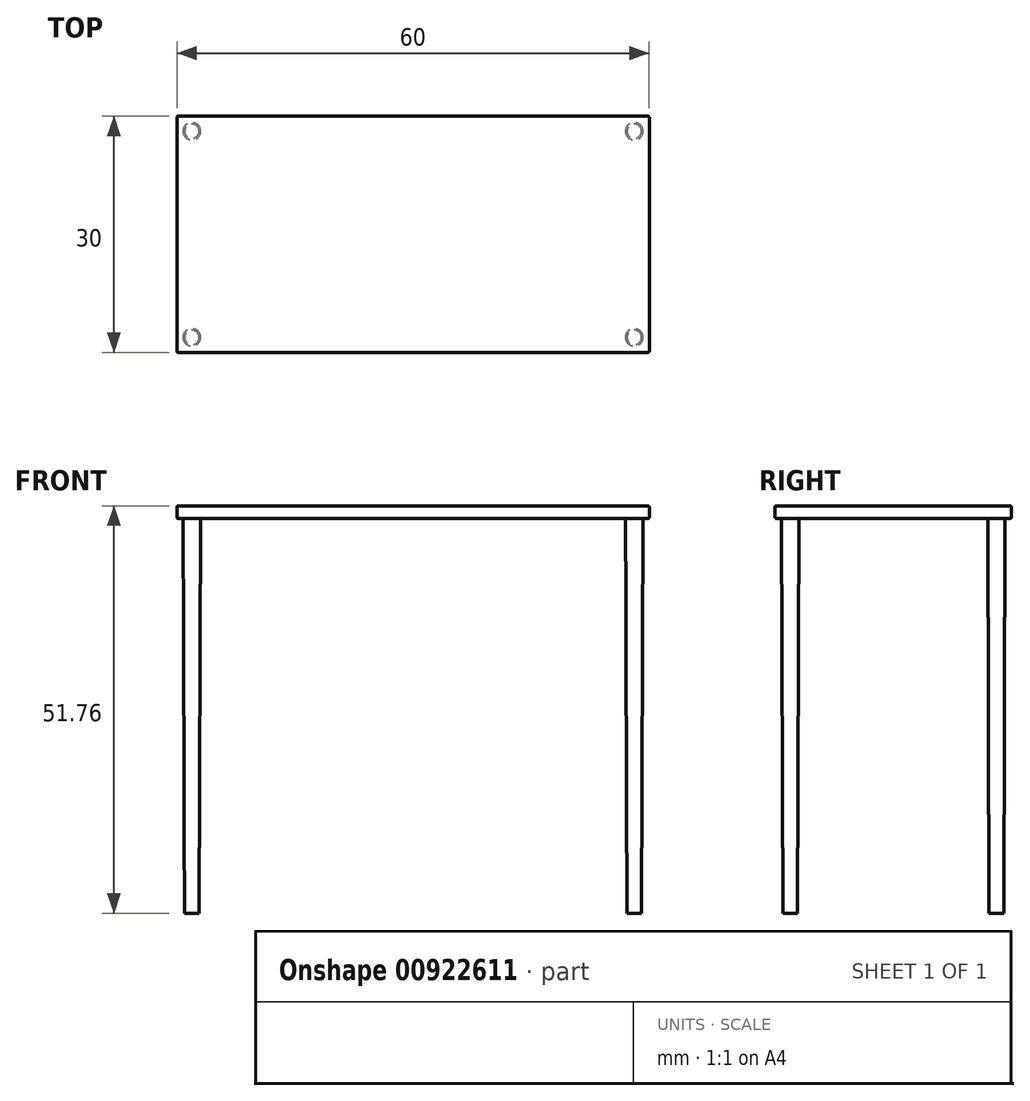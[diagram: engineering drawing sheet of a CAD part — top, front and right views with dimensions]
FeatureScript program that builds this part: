
annotation { "Feature Type Name" : "Feature", "Feature Type Description" : "" }
export const myFeature = defineFeature(function(context is Context, id is Id, definition is map)
    precondition{}
    {
        {
            var Q0;
            Q0=qCreatedBy(makeId("Top.planeOp"),FACE);
            var sketch = newSketch(context, id + "F0", { "sketchPlane" : qUnion([Q0])});
            skLineSegment(sketch, "E0.bottom", {"start": v(-600.08, 300.04) * mm, "end": v(600.08, 300.04) * mm});
            skLineSegment(sketch, "E0.top", {"start": v(-600.08, -300.04) * mm, "end": v(600.08, -300.04) * mm});
            skLineSegment(sketch, "E0.left", {"start": v(-600.07, 300.04) * mm, "end": v(-600.08, -300.04) * mm});
            skLineSegment(sketch, "E0.right", {"start": v(600.08, 300.04) * mm, "end": v(600.08, -300.04) * mm});
            skPoint(sketch, "E0.middle", {"position": v(0, 0) * mm});
            skSolve(sketch);
        }
        {
            var Q0;
            Q0 = qSketchRegion(id + "F0", true);
            extrude(context, id + "F1", {"entities" : qUnion([Q0]), "depth" : 31.75 * mm, "offsetDistance" : 25.4 * mm});
        }
        {
            var Q0;
            Q0=makeQuery(id+"F1.opExtrude","SWEPT_FACE",FACE,{"disambiguationData":[OSD([sQuery(id+"F0.wireOp",EDGE,"E0.bottom")])]});
            var Q1;
            Q1=makeQuery(id+"F1.opExtrude","CAP_FACE",FACE,{"disambiguationData":[OSD([sQuery(id+"F0.wireOp",EDGE,"E0.bottom"),sQuery(id+"F0.wireOp",EDGE,"E0.top"),sQuery(id+"F0.wireOp",EDGE,"E0.left"),sQuery(id+"F0.wireOp",EDGE,"E0.right")])],"isStart":true});
            var Q2;
            Q2=makeQuery(id+"F1.opExtrude","CAP_FACE",FACE,{"disambiguationData":[OSD([sQuery(id+"F0.wireOp",EDGE,"E0.bottom"),sQuery(id+"F0.wireOp",EDGE,"E0.top"),sQuery(id+"F0.wireOp",EDGE,"E0.left"),sQuery(id+"F0.wireOp",EDGE,"E0.right")])],"isStart":false});
            var Q3;
            Q3=makeQuery(id+"F1.opExtrude","SWEPT_FACE",FACE,{"disambiguationData":[OSD([sQuery(id+"F0.wireOp",EDGE,"E0.top")])]});
            var Q4;
            Q4=makeQuery(id+"F1.opExtrude","SWEPT_FACE",FACE,{"disambiguationData":[OSD([sQuery(id+"F0.wireOp",EDGE,"E0.left")])]});
            var Q5;
            Q5=makeQuery(id+"F1.opExtrude","CAP_EDGE",EDGE,{"disambiguationData":[OSD([sQuery(id+"F0.wireOp",EDGE,"E0.bottom")])],"isStart":false});
            var Q6;
            Q6=makeQuery(id+"F1.opExtrude","SWEPT_FACE",FACE,{"disambiguationData":[OSD([sQuery(id+"F0.wireOp",EDGE,"E0.right")])]});
            var Q7;
            Q7=makeQuery(id+"F1.opExtrude","CAP_EDGE",EDGE,{"disambiguationData":[OSD([sQuery(id+"F0.wireOp",EDGE,"E0.left")])],"isStart":true});
            var Q8;
            Q8=makeQuery(id+"F1.opExtrude","SWEPT_EDGE",EDGE,{"disambiguationData":[OSD([sQuery(id+"F0.wireOp",EDGE,"E0.bottom"),sQuery(id+"F0.wireOp",EDGE,"E0.left")])]});
            var Q9;
            Q9=makeQuery(id+"F1.opExtrude","SWEPT_EDGE",EDGE,{"disambiguationData":[OSD([sQuery(id+"F0.wireOp",EDGE,"E0.bottom"),sQuery(id+"F0.wireOp",EDGE,"E0.right")])]});
            var Q10;
            Q10=makeQuery(id+"F1.opExtrude","SWEPT_EDGE",EDGE,{"disambiguationData":[OSD([sQuery(id+"F0.wireOp",EDGE,"E0.top"),sQuery(id+"F0.wireOp",EDGE,"E0.left")])]});
            var Q11;
            Q11=makeQuery(id+"F1.opExtrude","SWEPT_EDGE",EDGE,{"disambiguationData":[OSD([sQuery(id+"F0.wireOp",EDGE,"E0.top"),sQuery(id+"F0.wireOp",EDGE,"E0.right")])]});
            var Q12;
            Q12=makeQuery(id+"F1.opExtrude","CAP_EDGE",EDGE,{"disambiguationData":[OSD([sQuery(id+"F0.wireOp",EDGE,"E0.bottom")])],"isStart":true});
            var Q13;
            Q13=makeQuery(id+"F1.opExtrude","CAP_EDGE",EDGE,{"disambiguationData":[OSD([sQuery(id+"F0.wireOp",EDGE,"E0.top")])],"isStart":true});
            var Q14;
            Q14=makeQuery(id+"F1.opExtrude","CAP_EDGE",EDGE,{"disambiguationData":[OSD([sQuery(id+"F0.wireOp",EDGE,"E0.top")])],"isStart":false});
            var Q15;
            Q15=makeQuery(id+"F1.opExtrude","CAP_EDGE",EDGE,{"disambiguationData":[OSD([sQuery(id+"F0.wireOp",EDGE,"E0.left")])],"isStart":false});
            var Q16;
            Q16=makeQuery(id+"F1.opExtrude","CAP_EDGE",EDGE,{"disambiguationData":[OSD([sQuery(id+"F0.wireOp",EDGE,"E0.right")])],"isStart":true});
            var Q17;
            Q17=makeQuery(id+"F1.opExtrude","CAP_EDGE",EDGE,{"disambiguationData":[OSD([sQuery(id+"F0.wireOp",EDGE,"E0.right")])],"isStart":false});
            fillet(context, id + "F2", {"entities" : qUnion([Q0, Q1, Q2, Q3, Q4, Q5, Q6, Q7, Q8, Q9, Q10, Q11, Q12, Q13, Q14, Q15, Q16, Q17]), "radius" : 2.54 * mm, "tangentPropagation" : true, "allowEdgeOverflow" : false});
        }
        {
            var Q0;
            Q0=makeQuery(id+"F1.opExtrude","CAP_FACE",FACE,{"disambiguationData":[OSD([sQuery(id+"F0.wireOp",EDGE,"E0.bottom"),sQuery(id+"F0.wireOp",EDGE,"E0.top"),sQuery(id+"F0.wireOp",EDGE,"E0.left"),sQuery(id+"F0.wireOp",EDGE,"E0.right")])],"isStart":true});
            var sketch = newSketch(context, id + "F3", { "sketchPlane" : qUnion([Q0])});
            skLineSegment(sketch, "E1.bottom", {"start": v(-561.97, 261.94) * mm, "end": v(561.97, 261.94) * mm, "construction": true});
            skLineSegment(sketch, "E1.top", {"start": v(-561.97, -261.94) * mm, "end": v(561.97, -261.94) * mm, "construction": true});
            skLineSegment(sketch, "E1.left", {"start": v(-561.97, 261.94) * mm, "end": v(-561.97, -261.94) * mm, "construction": true});
            skLineSegment(sketch, "E1.right", {"start": v(561.97, 261.94) * mm, "end": v(561.97, -261.94) * mm, "construction": true});
            skPoint(sketch, "E1.middle", {"position": v(0, 0) * mm});
            skCircle(sketch, "E2", {"center": v(-561.97, 261.94) * mm, "radius": 22.1 * mm});
            skCircle(sketch, "E3", {"center": v(561.97, 261.94) * mm, "radius": 22.1 * mm});
            skCircle(sketch, "E4", {"center": v(-561.97, -261.94) * mm, "radius": 22.1 * mm});
            skCircle(sketch, "E5", {"center": v(561.97, -261.94) * mm, "radius": 22.1 * mm});
            skSolve(sketch);
        }
        {
            var Q0;
            Q0 = qSketchRegion(id + "F3", true);
            extrude(context, id + "F4", {"entities" : qUnion([Q0]), "operationType" : NewBodyOperationType.ADD, "depth" : 1003.3 * mm, "offsetDistance" : 25.4 * mm, "hasDraft" : true, "draftAngle" : 0.2 * degree, "draftPullDirection" : true});
        }
        {
            var Q0;
            Q0=makeQuery(id+"F1.opExtrude","SWEPT_BODY",BODY,{"disambiguationData":[OSD([sQuery(id+"F0.wireOp",EDGE,"E0.bottom"),sQuery(id+"F0.wireOp",EDGE,"E0.top"),sQuery(id+"F0.wireOp",EDGE,"E0.left"),sQuery(id+"F0.wireOp",EDGE,"E0.right")])]});
            var Q1;
            Q1=qCreatedBy(makeId("Origin.pointOp"),VERTEX);
            transform(context, id + "F5", {"entities" : qUnion([Q0]), "transformType" : TransformType.SCALE_UNIFORMLY, "scale" : 0.05, "scalePoint" : qUnion([Q1]), "makeCopy" : false});
        }
    });
